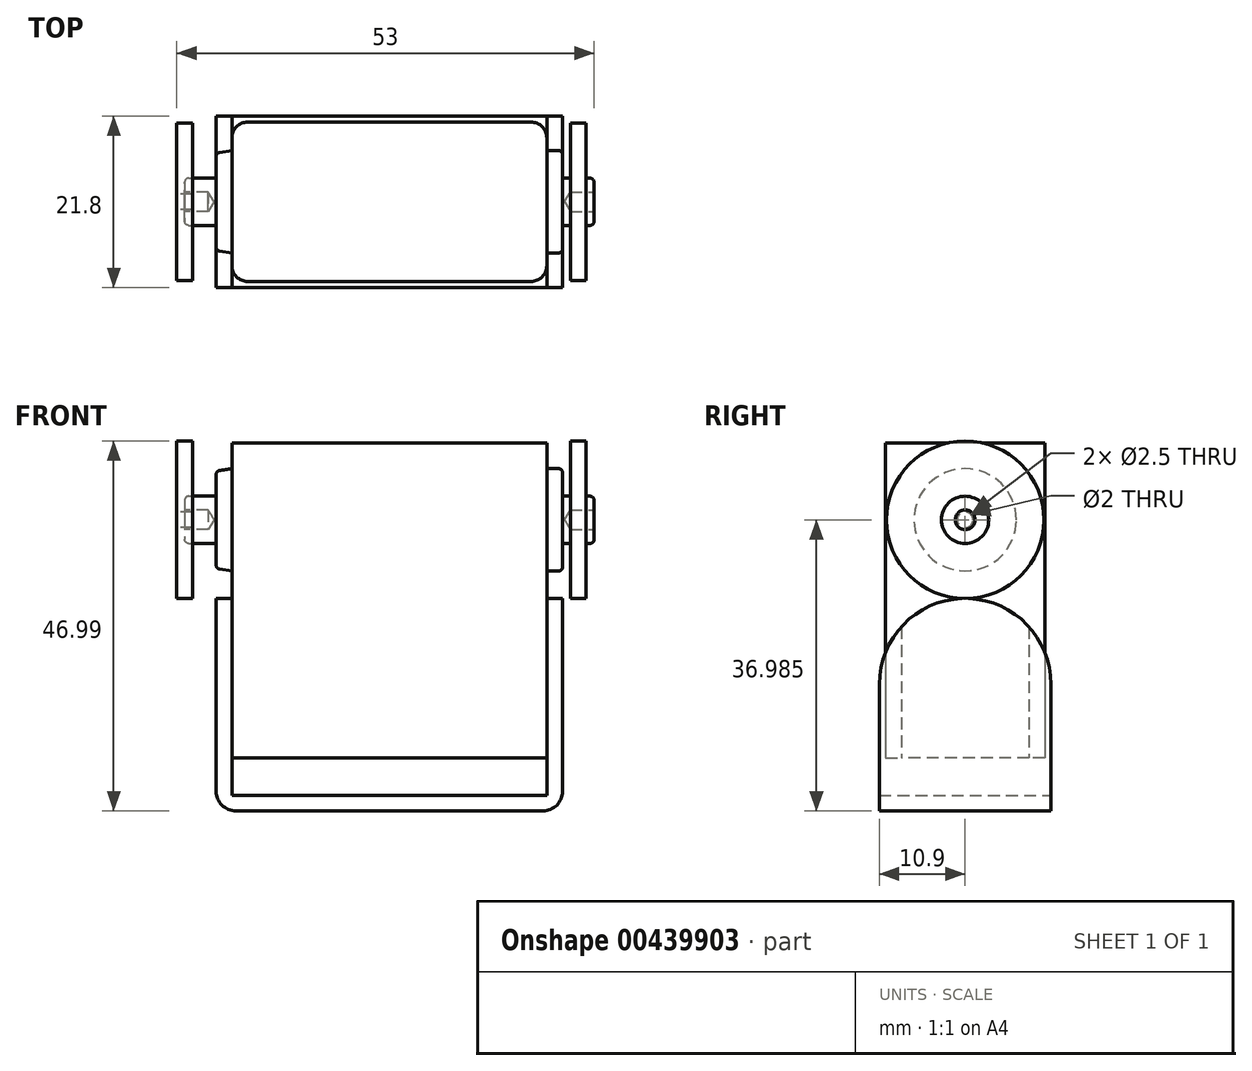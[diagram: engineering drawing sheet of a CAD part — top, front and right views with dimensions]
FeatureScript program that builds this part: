
annotation { "Feature Type Name" : "Feature", "Feature Type Description" : "" }
export const myFeature = defineFeature(function(context is Context, id is Id, definition is map)
    precondition{}
    {
        {
            var Q0;
            Q0=qCreatedBy(makeId("Top.planeOp"),FACE);
            var sketch = newSketch(context, id + "F0", { "sketchPlane" : qUnion([Q0])});
            skLineSegment(sketch, "E0.bottom", {"start": v(-20, 10.12) * mm, "end": v(20, 10.12) * mm});
            skLineSegment(sketch, "E0.top", {"start": v(-20, -10.12) * mm, "end": v(20, -10.12) * mm});
            skLineSegment(sketch, "E0.left", {"start": v(-20, 10.12) * mm, "end": v(-20, -10.12) * mm});
            skLineSegment(sketch, "E0.right", {"start": v(20, 10.12) * mm, "end": v(20, -10.12) * mm});
            skLineSegment(sketch, "E1", {"start": v(20, 10.13) * mm, "end": v(-20, -10.13) * mm, "construction": true});
            skSolve(sketch);
        }
        {
            var Q0;
            Q0=makeQuery(id+"F0.imprint","IMPRINT",FACE,{"disambiguationData":[TD([[makeQuery(id+"F0.imprint","IMPRINT",EDGE,{"derivedFrom":sQuery(id+"F0.wireOp",EDGE,"E0.bottom")}),-1.0]])]});
            extrude(context, id + "F1", {"entities" : qUnion([Q0]), "depth" : 40 * mm});
        }
        {
            var Q0;
            Q0=makeQuery(id+"F1.opExtrude","SWEPT_EDGE",EDGE,{"disambiguationData":[OSD([sQuery(id+"F0.wireOp",EDGE,"E0.bottom"),sQuery(id+"F0.wireOp",EDGE,"E0.left")])]});
            var Q1;
            Q1=makeQuery(id+"F1.opExtrude","SWEPT_EDGE",EDGE,{"disambiguationData":[OSD([sQuery(id+"F0.wireOp",EDGE,"E0.top"),sQuery(id+"F0.wireOp",EDGE,"E0.left")])]});
            var Q2;
            Q2=makeQuery(id+"F1.opExtrude","SWEPT_EDGE",EDGE,{"disambiguationData":[OSD([sQuery(id+"F0.wireOp",EDGE,"E0.bottom"),sQuery(id+"F0.wireOp",EDGE,"E0.right")])]});
            var Q3;
            Q3=makeQuery(id+"F1.opExtrude","SWEPT_EDGE",EDGE,{"disambiguationData":[OSD([sQuery(id+"F0.wireOp",EDGE,"E0.top"),sQuery(id+"F0.wireOp",EDGE,"E0.right")])]});
            fillet(context, id + "F2", {"entities" : qUnion([Q0, Q1, Q2, Q3]), "radius" : 2 * mm, "tangentPropagation" : true, "allowEdgeOverflow" : false});
        }
        {
            var Q0;
            Q0=makeQuery(id+"F1.opExtrude","SWEPT_FACE",FACE,{"disambiguationData":[OSD([sQuery(id+"F0.wireOp",EDGE,"E0.left")])]});
            var sketch = newSketch(context, id + "F3", { "sketchPlane" : qUnion([Q0])});
            skCircle(sketch, "E2", {"center": v(0, 30.23) * mm, "radius": 6.5 * mm});
            skPoint(sketch, "E3.endSnap0", {"position": v(0, 40) * mm});
            skLineSegment(sketch, "E4", {"start": v(0, 0) * mm, "end": v(0, 30.23) * mm, "construction": true});
            skSolve(sketch);
        }
        {
            var Q0;
            Q0=makeQuery(id+"F3.imprint","IMPRINT",FACE,{"disambiguationData":[TD([[makeQuery(id+"F3.imprint","IMPRINT",EDGE,{"derivedFrom":sQuery(id+"F3.wireOp",EDGE,"E2")}),1.0]])]});
            var Q1;
            Q1=sQuery(id+"F3.wireOp",EDGE,"E2");
            extrude(context, id + "F4", {"entities" : qUnion([Q0]), "operationType" : NewBodyOperationType.ADD, "surfaceEntities" : qUnion([Q1]), "depth" : 2 * mm});
        }
        {
            var Q0;
            Q0=makeQuery(id+"F4.opExtrude","CAP_FACE",FACE,{"disambiguationData":[OSD([sQuery(id+"F3.wireOp",EDGE,"E2")])],"isStart":false});
            chamfer(context, id + "F5", {"entities" : qUnion([Q0]), "chamferType" : ChamferType.TWO_OFFSETS, "width1" : 2 * mm, "oppositeDirection" : true, "width2" : 0.3 * mm, "tangentPropagation" : true});
        }
        {
            var Q0;
            {var subQ0=sQuery(id+"F3.wireOp",EDGE,"E2");Q0=makeQuery(id+"F5.opChamfer","BLEND_EDGE",EDGE,{"blendedFrom":[makeQuery(id+"F4.opExtrude","CAP_EDGE",EDGE,{"disambiguationData":[OSD([subQ0])],"isStart":false}),makeQuery(id+"F4.opExtrude","CAP_FACE",FACE,{"disambiguationData":[OSD([subQ0])],"isStart":false})],"blendedInto":[makeQuery(id+"F4.opExtrude","CAP_FACE",FACE,{"disambiguationData":[OSD([subQ0])],"isStart":false})]});}
            fillet(context, id + "F6", {"entities" : qUnion([Q0]), "radius" : 0.5 * mm, "tangentPropagation" : true, "allowEdgeOverflow" : false});
        }
        {
            var Q0;
            Q0=makeQuery(id+"F4.opExtrude","CAP_FACE",FACE,{"disambiguationData":[OSD([sQuery(id+"F3.wireOp",EDGE,"E2")])],"isStart":false});
            var sketch = newSketch(context, id + "F7", { "sketchPlane" : qUnion([Q0])});
            skCircle(sketch, "E5", {"center": v(0, 30.23) * mm, "radius": 3 * mm});
            skSolve(sketch);
        }
        {
            var Q0;
            Q0=qSketchRegion(id+"F7",true);
            extrude(context, id + "F8", {"entities" : qUnion([Q0]), "operationType" : NewBodyOperationType.ADD, "depth" : 4 * mm});
        }
        {
            var Q0;
            Q0=makeQuery(id+"F8.opExtrude","CAP_EDGE",EDGE,{"disambiguationData":[OSD([sQuery(id+"F7.wireOp",EDGE,"E5")])],"isStart":false});
            fillet(context, id + "F9", {"entities" : qUnion([Q0]), "radius" : 0.5 * mm, "tangentPropagation" : true, "allowEdgeOverflow" : false});
        }
        {
            var Q0;
            Q0=makeQuery(id+"F1.opExtrude","SWEPT_FACE",FACE,{"disambiguationData":[OSD([sQuery(id+"F0.wireOp",EDGE,"E0.right")])]});
            var sketch = newSketch(context, id + "F10", { "sketchPlane" : qUnion([Q0])});
            skPoint(sketch, "E6.endSnap0", {"position": v(0, 40) * mm});
            skCircle(sketch, "E7", {"center": v(0, 30.23) * mm, "radius": 6.5 * mm});
            skLineSegment(sketch, "E8", {"start": v(0, 0) * mm, "end": v(0, 30.23) * mm, "construction": true});
            skSolve(sketch);
        }
        {
            var Q0;
            Q0=qSketchRegion(id+"F10",true);
            extrude(context, id + "F11", {"entities" : qUnion([Q0]), "operationType" : NewBodyOperationType.ADD, "depth" : 2 * mm});
        }
        {
            var Q0;
            Q0=makeQuery(id+"F11.opExtrude","CAP_EDGE",EDGE,{"disambiguationData":[OSD([sQuery(id+"F10.wireOp",EDGE,"E7")])],"isStart":false});
            fillet(context, id + "F12", {"entities" : qUnion([Q0]), "radius" : 0.5 * mm, "tangentPropagation" : true, "allowEdgeOverflow" : false});
        }
        {
            var Q0;
            Q0=makeQuery(id+"F11.opExtrude","CAP_FACE",FACE,{"disambiguationData":[OSD([sQuery(id+"F10.wireOp",EDGE,"E7")])],"isStart":false});
            var sketch = newSketch(context, id + "F13", { "sketchPlane" : qUnion([Q0])});
            skCircle(sketch, "E9", {"center": v(0, 30.23) * mm, "radius": 3 * mm});
            skSolve(sketch);
        }
        {
            var Q0;
            Q0=qSketchRegion(id+"F13",true);
            extrude(context, id + "F14", {"entities" : qUnion([Q0]), "operationType" : NewBodyOperationType.ADD, "depth" : 4 * mm});
        }
        {
            var Q0;
            Q0=makeQuery(id+"F14.opExtrude","CAP_EDGE",EDGE,{"disambiguationData":[OSD([sQuery(id+"F13.wireOp",EDGE,"E9")])],"isStart":false});
            fillet(context, id + "F15", {"entities" : qUnion([Q0]), "radius" : 0.5 * mm, "tangentPropagation" : true, "allowEdgeOverflow" : false});
        }
        {
            var Q0;
            Q0=makeQuery(id+"F8.opExtrude","CAP_FACE",FACE,{"disambiguationData":[OSD([sQuery(id+"F7.wireOp",EDGE,"E5")])],"isStart":false});
            var sketch = newSketch(context, id + "F16", { "sketchPlane" : qUnion([Q0])});
            skCircle(sketch, "E10", {"center": v(0, 30.23) * mm, "radius": 1.02 * mm, "construction": true});
            skSolve(sketch);
        }
        {
            var Q0;
            Q0=sQuery(id+"F16.wireOp",VERTEX,"E10.center");
            var Q1;
            Q1=makeQuery(id+"F1.opExtrude","SWEPT_BODY",BODY,{"disambiguationData":[OSD([sQuery(id+"F0.wireOp",EDGE,"E0.bottom"),sQuery(id+"F0.wireOp",EDGE,"E0.top"),sQuery(id+"F0.wireOp",EDGE,"E0.left"),sQuery(id+"F0.wireOp",EDGE,"E0.right")])]});
            hole(context, id + "F17", {"style" : HoleStyle.C_BORE, "endStyle" : HoleEndStyle.BLIND, "holeDiameter" : 2.5 * mm, "cBoreDiameter" : 2.5 * mm, "cBoreDepth" : 0 * mm, "holeDepth" : 3 * mm, "isTappedThrough" : true, "tappedDepth" : 12 * mm, "tapClearance" : 3, "startFromSketch" : true, "locations" : qUnion([Q0]), "scope" : qUnion([Q1])});
        }
        {
            var Q0;
            Q0=makeQuery(id+"F14.opExtrude","CAP_FACE",FACE,{"disambiguationData":[OSD([sQuery(id+"F13.wireOp",EDGE,"E9")])],"isStart":false});
            var sketch = newSketch(context, id + "F18", { "sketchPlane" : qUnion([Q0])});
            skCircle(sketch, "E11", {"center": v(0, 30.23) * mm, "radius": 0.97 * mm, "construction": true});
            skSolve(sketch);
        }
        {
            var Q0;
            Q0=sQuery(id+"F18.wireOp",VERTEX,"E11.center");
            var Q1;
            Q1=makeQuery(id+"F1.opExtrude","SWEPT_BODY",BODY,{"disambiguationData":[OSD([sQuery(id+"F0.wireOp",EDGE,"E0.bottom"),sQuery(id+"F0.wireOp",EDGE,"E0.top"),sQuery(id+"F0.wireOp",EDGE,"E0.left"),sQuery(id+"F0.wireOp",EDGE,"E0.right")])]});
            hole(context, id + "F19", {"style" : HoleStyle.C_BORE, "endStyle" : HoleEndStyle.BLIND, "holeDiameter" : 2.5 * mm, "cBoreDiameter" : 2.5 * mm, "cBoreDepth" : 0 * mm, "holeDepth" : 3 * mm, "isTappedThrough" : true, "tappedDepth" : 12 * mm, "tapClearance" : 3, "startFromSketch" : true, "locations" : qUnion([Q0]), "scope" : qUnion([Q1])});
        }
        {
            var Q0;
            Q0=makeQuery(id+"F1.opExtrude","SWEPT_FACE",FACE,{"disambiguationData":[OSD([sQuery(id+"F0.wireOp",EDGE,"E0.left")])]});
            cPlane(context, id + "F20", {"entities" : qUnion([Q0]), "cplaneType" : CPlaneType.OFFSET, "offset" : 7 * mm, "width" : 150 * mm, "height" : 150 * mm});
        }
        {
            var Q0;
            Q0=qCreatedBy(id+"F20.planeOp",FACE);
            var sketch = newSketch(context, id + "F21", { "sketchPlane" : qUnion([Q0])});
            skCircle(sketch, "E12", {"center": v(0, 30.23) * mm, "radius": 10 * mm});
            skCircle(sketch, "E13", {"center": v(0, 30.23) * mm, "radius": 1 * mm});
            skLineSegment(sketch, "E14", {"start": v(0, 0) * mm, "end": v(0, 30.23) * mm, "construction": true});
            skSolve(sketch);
        }
        {
            var Q0;
            Q0=qSketchRegion(id+"F21",true);
            extrude(context, id + "F22", {"entities" : qUnion([Q0]), "oppositeDirection" : true, "depth" : 2 * mm});
        }
        {
            var Q0;
            Q0=makeQuery(id+"F1.opExtrude","SWEPT_FACE",FACE,{"disambiguationData":[OSD([sQuery(id+"F0.wireOp",EDGE,"E0.right")])]});
            cPlane(context, id + "F23", {"entities" : qUnion([Q0]), "cplaneType" : CPlaneType.OFFSET, "offset" : 5 * mm, "width" : 150 * mm, "height" : 150 * mm});
        }
        {
            var Q0;
            Q0=qCreatedBy(id+"F23.planeOp",FACE);
            var sketch = newSketch(context, id + "F24", { "sketchPlane" : qUnion([Q0])});
            skLineSegment(sketch, "E15", {"start": v(0, 0) * mm, "end": v(0, 30.23) * mm, "construction": true});
            skCircle(sketch, "E16", {"center": v(0, 30.23) * mm, "radius": 10 * mm});
            skCircle(sketch, "E17", {"center": v(0, 30.23) * mm, "radius": 3 * mm});
            skSolve(sketch);
        }
        {
            var Q0;
            Q0=qSketchRegion(id+"F24",true);
            extrude(context, id + "F25", {"entities" : qUnion([Q0]), "operationType" : NewBodyOperationType.ADD, "oppositeDirection" : true, "depth" : 2 * mm});
        }
        {
            var Q0;
            Q0=qCreatedBy(makeId("Front.planeOp"),FACE);
            var sketch = newSketch(context, id + "F26", { "sketchPlane" : qUnion([Q0])});
            skLineSegment(sketch, "E18.top", {"start": v(22, 20.24) * mm, "end": v(20, 20.24) * mm});
            skLineSegment(sketch, "E18.left", {"start": v(20, -4.76) * mm, "end": v(20, 20.24) * mm});
            skLineSegment(sketch, "E18.right", {"start": v(-20, -4.76) * mm, "end": v(-20, 20.24) * mm});
            skLineSegment(sketch, "E19", {"start": v(22, -6.76) * mm, "end": v(22, 20.24) * mm});
            skLineSegment(sketch, "E20", {"start": v(-22, -6.76) * mm, "end": v(-22, 20.24) * mm});
            skLineSegment(sketch, "E21", {"start": v(22, -6.76) * mm, "end": v(-22, -6.76) * mm});
            skLineSegment(sketch, "E22.trimOffspring", {"start": v(-20, 20.24) * mm, "end": v(-22, 20.24) * mm});
            skLineSegment(sketch, "E23", {"start": v(20, -4.76) * mm, "end": v(-20, -4.76) * mm});
            skLineSegment(sketch, "E24", {"start": v(0, -16.38) * mm, "end": v(0, 40) * mm, "construction": true});
            skLineSegment(sketch, "E25", {"start": v(70.06, 114.57) * mm, "end": v(41.2, 114.57) * mm, "construction": true});
            skLineSegment(sketch, "E26", {"start": v(55.5, 154.8) * mm, "end": v(36.18, 154.8) * mm, "construction": true});
            skLineSegment(sketch, "E27", {"start": v(37.78, 20.24) * mm, "end": v(20, 20.24) * mm, "construction": true});
            skSolve(sketch);
        }
        {
            var Q0;
            Q0=makeQuery(id+"F26.imprint","IMPRINT",FACE,{"disambiguationData":[TD([[makeQuery(id+"F26.imprint","IMPRINT",EDGE,{"derivedFrom":sQuery(id+"F26.wireOp",EDGE,"E18.top")}),1.0]])]});
            extrude(context, id + "F27", {"entities" : qUnion([Q0]), "operationType" : NewBodyOperationType.ADD, "endBound" : BoundingType.SYMMETRIC, "depth" : 21.8 * mm, "offsetDistance" : 25 * mm});
        }
        {
            var Q0;
            Q0=makeQuery(id+"F27.opExtrude","CAP_EDGE",EDGE,{"disambiguationData":[OSD([sQuery(id+"F26.wireOp",EDGE,"E18.top")])],"isStart":true});
            var Q1;
            Q1=makeQuery(id+"F27.opExtrude","CAP_EDGE",EDGE,{"disambiguationData":[OSD([sQuery(id+"F26.wireOp",EDGE,"E18.top")])],"isStart":false});
            var Q2;
            Q2=makeQuery(id+"F27.opExtrude","CAP_EDGE",EDGE,{"disambiguationData":[OSD([sQuery(id+"F26.wireOp",EDGE,"E22.trimOffspring")])],"isStart":true});
            var Q3;
            Q3=makeQuery(id+"F27.opExtrude","CAP_EDGE",EDGE,{"disambiguationData":[OSD([sQuery(id+"F26.wireOp",EDGE,"E22.trimOffspring")])],"isStart":false});
            fillet(context, id + "F28", {"entities" : qUnion([Q0, Q1, Q2, Q3]), "radius" : (21.8 / 2) * mm, "tangentPropagation" : true, "allowEdgeOverflow" : false});
        }
        {
            var Q0;
            Q0=makeQuery(id+"F27.opExtrude","SWEPT_EDGE",EDGE,{"disambiguationData":[OSD([sQuery(id+"F26.wireOp",EDGE,"E19"),sQuery(id+"F26.wireOp",EDGE,"E21")])]});
            var Q1;
            Q1=makeQuery(id+"F27.opExtrude","SWEPT_EDGE",EDGE,{"disambiguationData":[OSD([sQuery(id+"F26.wireOp",EDGE,"E20"),sQuery(id+"F26.wireOp",EDGE,"E21")])]});
            fillet(context, id + "F29", {"entities" : qUnion([Q0, Q1]), "radius" : 2.5 * mm, "tangentPropagation" : true, "allowEdgeOverflow" : false});
        }
        {
            var Q0;
            Q0=makeQuery(id+"F27.opExtrude","SWEPT_FACE",FACE,{"disambiguationData":[OSD([sQuery(id+"F26.wireOp",EDGE,"E21")])]});
            var sketch = newSketch(context, id + "F30", { "sketchPlane" : qUnion([Q0])});
            skLineSegment(sketch, "E28", {"start": v(-22.1, 0) * mm, "end": v(22.1, 0) * mm, "construction": true});
            skCircle(sketch, "E29.1.0.0", {"center": v(-5, 5) * mm, "radius": 1.24 * mm});
            skCircle(sketch, "E29.1.1.0", {"center": v(-5, -5) * mm, "radius": 1.24 * mm});
            skCircle(sketch, "E29.2.0.0", {"center": v(5, 5) * mm, "radius": 1.24 * mm});
            skCircle(sketch, "E29.2.1.0", {"center": v(5, -5) * mm, "radius": 1.24 * mm});
            skLineSegment(sketch, "E30", {"start": v(-5, 5) * mm, "end": v(5, -5) * mm, "construction": true});
            skLineSegment(sketch, "E31", {"start": v(-10, 0) * mm, "end": v(-5, 5) * mm, "construction": true});
            skLineSegment(sketch, "E32", {"start": v(0, 0) * mm, "end": v(0, 19.74) * mm, "construction": true});
            skPoint(sketch, "E32.endSnap0", {"position": v(0, 10.9) * mm});
            skLineSegment(sketch, "E33.MirrorCS", {"start": v(10, 0) * mm, "end": v(5, 5) * mm, "construction": true});
            skCircle(sketch, "E34.1.0.0", {"center": v(-11.24, 0) * mm, "radius": 1.24 * mm});
            skCircle(sketch, "E35.MirrorC", {"center": v(11.24, 0) * mm, "radius": 1.24 * mm});
            skSolve(sketch);
        }
        {
            var Q0;
            Q0=sQuery(id+"F30.wireOp",VERTEX,"E30.start");
            var Q1;
            Q1=sQuery(id+"F30.wireOp",VERTEX,"E29.1.1.0.center");
            var Q2;
            Q2=sQuery(id+"F30.wireOp",VERTEX,"E30.end");
            var Q3;
            Q3=sQuery(id+"F30.wireOp",VERTEX,"E33.MirrorCS.end");
            var Q4;
            Q4=makeQuery(id+"F22.opExtrude","SWEPT_BODY",BODY,{"disambiguationData":[OSD([sQuery(id+"F21.wireOp",EDGE,"E12"),sQuery(id+"F21.wireOp",EDGE,"E13")])]});
            hole(context, id + "F31", {"style" : HoleStyle.SIMPLE, "endStyle" : HoleEndStyle.BLIND, "holeDiameter" : 3 * mm, "majorDiameter" : 5 * mm, "holeDepth" : 3 * mm, "isTappedThrough" : true, "tappedDepth" : 12 * mm, "tapClearance" : 3, "startFromSketch" : true, "locations" : qUnion([Q0, Q1, Q2, Q3]), "scope" : qUnion([Q4])});
        }
    });
